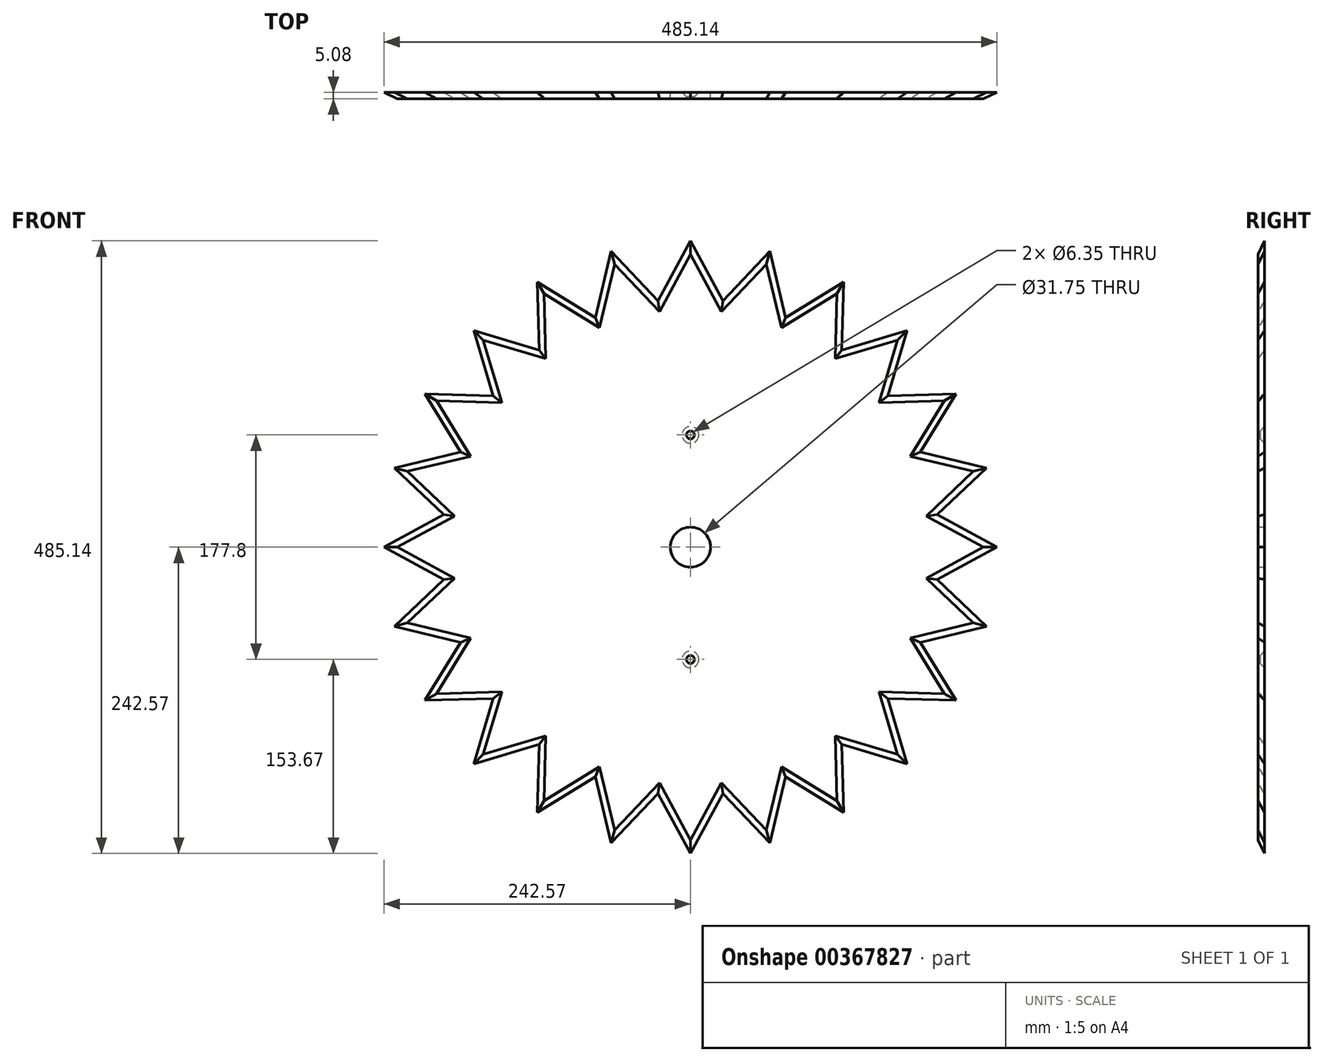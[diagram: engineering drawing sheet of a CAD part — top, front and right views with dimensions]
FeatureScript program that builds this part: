
annotation { "Feature Type Name" : "Feature", "Feature Type Description" : "" }
export const myFeature = defineFeature(function(context is Context, id is Id, definition is map)
    precondition{}
    {
        {
            var Q0;
            Q0=qCreatedBy(makeId("Front.planeOp"),FACE);
            var sketch = newSketch(context, id + "F0", { "sketchPlane" : qUnion([Q0])});
            skCircle(sketch, "E0", {"center": v(0, 0) * mm, "radius": 196.85 * mm});
            skLineSegment(sketch, "E1", {"start": v(0, 0) * mm, "end": v(0, 196.85) * mm, "construction": true});
            skLineSegment(sketch, "E2", {"start": v(0, 0) * mm, "end": v(50.95, 190.14) * mm, "construction": true});
            skLineSegment(sketch, "E3", {"start": v(0, 196.85) * mm, "end": v(0, 242.57) * mm, "construction": true});
            skLineSegment(sketch, "E4", {"start": v(0, 0) * mm, "end": v(25.7, 195.17) * mm, "construction": true});
            skLineSegment(sketch, "E5", {"start": v(0, 242.57) * mm, "end": v(25.7, 195.17) * mm});
            skLineSegment(sketch, "E6", {"start": v(50.95, 190.14) * mm, "end": v(62.78, 234.3) * mm, "construction": true});
            skLineSegment(sketch, "E7", {"start": v(25.7, 195.17) * mm, "end": v(62.78, 234.3) * mm});
            skLineSegment(sketch, "E8.1.0", {"start": v(62.78, 234.3) * mm, "end": v(75.33, 181.87) * mm});
            skLineSegment(sketch, "E8.1.1", {"start": v(75.33, 181.87) * mm, "end": v(121.28, 210.07) * mm});
            skLineSegment(sketch, "E8.2.0", {"start": v(121.29, 210.07) * mm, "end": v(119.83, 156.17) * mm});
            skLineSegment(sketch, "E8.2.1", {"start": v(119.83, 156.17) * mm, "end": v(171.52, 171.52) * mm});
            skLineSegment(sketch, "E8.3.0", {"start": v(171.52, 171.52) * mm, "end": v(156.17, 119.83) * mm});
            skLineSegment(sketch, "E8.3.1", {"start": v(156.17, 119.83) * mm, "end": v(210.07, 121.29) * mm});
            skLineSegment(sketch, "E8.4.0", {"start": v(210.07, 121.29) * mm, "end": v(181.87, 75.33) * mm});
            skLineSegment(sketch, "E8.4.1", {"start": v(181.87, 75.33) * mm, "end": v(234.3, 62.78) * mm});
            skLineSegment(sketch, "E8.5.0", {"start": v(234.3, 62.78) * mm, "end": v(195.17, 25.7) * mm});
            skLineSegment(sketch, "E8.5.1", {"start": v(195.17, 25.7) * mm, "end": v(242.57, 0) * mm});
            skLineSegment(sketch, "E8.6.0", {"start": v(242.57, 0) * mm, "end": v(195.17, -25.7) * mm});
            skLineSegment(sketch, "E8.6.1", {"start": v(195.17, -25.7) * mm, "end": v(234.3, -62.78) * mm});
            skLineSegment(sketch, "E8.7.0", {"start": v(234.3, -62.78) * mm, "end": v(181.87, -75.33) * mm});
            skLineSegment(sketch, "E8.7.1", {"start": v(181.87, -75.33) * mm, "end": v(210.07, -121.28) * mm});
            skLineSegment(sketch, "E8.8.0", {"start": v(210.07, -121.28) * mm, "end": v(156.17, -119.83) * mm});
            skLineSegment(sketch, "E8.8.1", {"start": v(156.17, -119.83) * mm, "end": v(171.52, -171.52) * mm});
            skLineSegment(sketch, "E8.9.0", {"start": v(171.52, -171.52) * mm, "end": v(119.83, -156.17) * mm});
            skLineSegment(sketch, "E8.9.1", {"start": v(119.83, -156.17) * mm, "end": v(121.29, -210.07) * mm});
            skLineSegment(sketch, "E8.10.0", {"start": v(121.29, -210.07) * mm, "end": v(75.33, -181.87) * mm});
            skLineSegment(sketch, "E8.10.1", {"start": v(75.33, -181.87) * mm, "end": v(62.78, -234.3) * mm});
            skLineSegment(sketch, "E8.11.0", {"start": v(62.78, -234.3) * mm, "end": v(25.7, -195.17) * mm});
            skLineSegment(sketch, "E8.11.1", {"start": v(25.7, -195.17) * mm, "end": v(0, -242.57) * mm});
            skLineSegment(sketch, "E8.12.0", {"start": v(0, -242.57) * mm, "end": v(-25.7, -195.17) * mm});
            skLineSegment(sketch, "E8.12.1", {"start": v(-25.7, -195.17) * mm, "end": v(-62.78, -234.3) * mm});
            skLineSegment(sketch, "E8.13.0", {"start": v(-62.78, -234.3) * mm, "end": v(-75.33, -181.87) * mm});
            skLineSegment(sketch, "E8.13.1", {"start": v(-75.33, -181.87) * mm, "end": v(-121.28, -210.07) * mm});
            skLineSegment(sketch, "E8.14.0", {"start": v(-121.28, -210.07) * mm, "end": v(-119.83, -156.17) * mm});
            skLineSegment(sketch, "E8.14.1", {"start": v(-119.83, -156.17) * mm, "end": v(-171.52, -171.52) * mm});
            skLineSegment(sketch, "E8.15.0", {"start": v(-171.52, -171.52) * mm, "end": v(-156.17, -119.83) * mm});
            skLineSegment(sketch, "E8.15.1", {"start": v(-156.17, -119.83) * mm, "end": v(-210.07, -121.29) * mm});
            skLineSegment(sketch, "E8.16.0", {"start": v(-210.07, -121.29) * mm, "end": v(-181.87, -75.33) * mm});
            skLineSegment(sketch, "E8.16.1", {"start": v(-181.87, -75.33) * mm, "end": v(-234.3, -62.78) * mm});
            skLineSegment(sketch, "E8.17.0", {"start": v(-234.3, -62.78) * mm, "end": v(-195.17, -25.7) * mm});
            skLineSegment(sketch, "E8.17.1", {"start": v(-195.17, -25.7) * mm, "end": v(-242.57, 0) * mm});
            skLineSegment(sketch, "E8.18.0", {"start": v(-242.57, 0) * mm, "end": v(-195.17, 25.7) * mm});
            skLineSegment(sketch, "E8.18.1", {"start": v(-195.17, 25.7) * mm, "end": v(-234.3, 62.78) * mm});
            skLineSegment(sketch, "E8.19.0", {"start": v(-234.3, 62.78) * mm, "end": v(-181.87, 75.33) * mm});
            skLineSegment(sketch, "E8.19.1", {"start": v(-181.87, 75.33) * mm, "end": v(-210.07, 121.29) * mm});
            skLineSegment(sketch, "E8.20.0", {"start": v(-210.07, 121.28) * mm, "end": v(-156.17, 119.83) * mm});
            skLineSegment(sketch, "E8.20.1", {"start": v(-156.17, 119.83) * mm, "end": v(-171.52, 171.52) * mm});
            skLineSegment(sketch, "E8.21.0", {"start": v(-171.52, 171.52) * mm, "end": v(-119.83, 156.17) * mm});
            skLineSegment(sketch, "E8.21.1", {"start": v(-119.83, 156.17) * mm, "end": v(-121.28, 210.07) * mm});
            skLineSegment(sketch, "E8.22.0", {"start": v(-121.29, 210.07) * mm, "end": v(-75.33, 181.87) * mm});
            skLineSegment(sketch, "E8.22.1", {"start": v(-75.33, 181.87) * mm, "end": v(-62.78, 234.3) * mm});
            skLineSegment(sketch, "E8.23.0", {"start": v(-62.78, 234.3) * mm, "end": v(-25.7, 195.17) * mm});
            skLineSegment(sketch, "E8.23.1", {"start": v(-25.7, 195.17) * mm, "end": v(0, 242.57) * mm});
            skLineSegment(sketch, "E8.anchor2", {"start": v(0, 0) * mm, "end": v(-25.7, 195.17) * mm, "construction": true});
            skSolve(sketch);
        }
        {
            var Q0;
            {var subQ0=sQuery(id+"F0.wireOp",EDGE,"E8.4.1");Q0=makeQuery(id+"F0.imprint","IMPRINT",FACE,{"disambiguationData":[TD([[makeQuery(id+"F0.imprint","IMPRINT",EDGE,{"derivedFrom":subQ0}),-1.0]])]});}
            var Q1;
            {var subQ0=sQuery(id+"F0.wireOp",EDGE,"E8.3.1");Q1=makeQuery(id+"F0.imprint","IMPRINT",FACE,{"disambiguationData":[TD([[makeQuery(id+"F0.imprint","IMPRINT",EDGE,{"derivedFrom":subQ0}),-1.0]])]});}
            var Q2;
            {var subQ0=sQuery(id+"F0.wireOp",EDGE,"E8.2.1");Q2=makeQuery(id+"F0.imprint","IMPRINT",FACE,{"disambiguationData":[TD([[makeQuery(id+"F0.imprint","IMPRINT",EDGE,{"derivedFrom":subQ0}),-1.0]])]});}
            var Q3;
            {var subQ0=sQuery(id+"F0.wireOp",EDGE,"E8.1.1");Q3=makeQuery(id+"F0.imprint","IMPRINT",FACE,{"disambiguationData":[TD([[makeQuery(id+"F0.imprint","IMPRINT",EDGE,{"derivedFrom":subQ0}),-1.0]])]});}
            var Q4;
            {var subQ0=sQuery(id+"F0.wireOp",EDGE,"E7");Q4=makeQuery(id+"F0.imprint","IMPRINT",FACE,{"disambiguationData":[TD([[makeQuery(id+"F0.imprint","IMPRINT",EDGE,{"derivedFrom":subQ0}),-1.0]])]});}
            var Q5;
            {var subQ0=sQuery(id+"F0.wireOp",EDGE,"E5");Q5=makeQuery(id+"F0.imprint","IMPRINT",FACE,{"disambiguationData":[TD([[makeQuery(id+"F0.imprint","IMPRINT",EDGE,{"derivedFrom":subQ0}),-1.0]])]});}
            var Q6;
            {var subQ0=sQuery(id+"F0.wireOp",EDGE,"E8.22.1");Q6=makeQuery(id+"F0.imprint","IMPRINT",FACE,{"disambiguationData":[TD([[makeQuery(id+"F0.imprint","IMPRINT",EDGE,{"derivedFrom":subQ0}),-1.0]])]});}
            var Q7;
            {var subQ0=sQuery(id+"F0.wireOp",EDGE,"E8.21.1");Q7=makeQuery(id+"F0.imprint","IMPRINT",FACE,{"disambiguationData":[TD([[makeQuery(id+"F0.imprint","IMPRINT",EDGE,{"derivedFrom":subQ0}),-1.0]])]});}
            var Q8;
            {var subQ0=sQuery(id+"F0.wireOp",EDGE,"E8.20.1");Q8=makeQuery(id+"F0.imprint","IMPRINT",FACE,{"disambiguationData":[TD([[makeQuery(id+"F0.imprint","IMPRINT",EDGE,{"derivedFrom":subQ0}),-1.0]])]});}
            var Q9;
            {var subQ0=sQuery(id+"F0.wireOp",EDGE,"E8.19.1");Q9=makeQuery(id+"F0.imprint","IMPRINT",FACE,{"disambiguationData":[TD([[makeQuery(id+"F0.imprint","IMPRINT",EDGE,{"derivedFrom":subQ0}),-1.0]])]});}
            var Q10;
            {var subQ0=sQuery(id+"F0.wireOp",EDGE,"E8.18.1");Q10=makeQuery(id+"F0.imprint","IMPRINT",FACE,{"disambiguationData":[TD([[makeQuery(id+"F0.imprint","IMPRINT",EDGE,{"derivedFrom":subQ0}),-1.0]])]});}
            var Q11;
            {var subQ0=sQuery(id+"F0.wireOp",EDGE,"E8.17.1");Q11=makeQuery(id+"F0.imprint","IMPRINT",FACE,{"disambiguationData":[TD([[makeQuery(id+"F0.imprint","IMPRINT",EDGE,{"derivedFrom":subQ0}),-1.0]])]});}
            var Q12;
            {var subQ0=sQuery(id+"F0.wireOp",EDGE,"E8.16.1");Q12=makeQuery(id+"F0.imprint","IMPRINT",FACE,{"disambiguationData":[TD([[makeQuery(id+"F0.imprint","IMPRINT",EDGE,{"derivedFrom":subQ0}),-1.0]])]});}
            var Q13;
            {var subQ0=sQuery(id+"F0.wireOp",EDGE,"E8.15.1");Q13=makeQuery(id+"F0.imprint","IMPRINT",FACE,{"disambiguationData":[TD([[makeQuery(id+"F0.imprint","IMPRINT",EDGE,{"derivedFrom":subQ0}),-1.0]])]});}
            var Q14;
            {var subQ0=sQuery(id+"F0.wireOp",EDGE,"E8.14.1");Q14=makeQuery(id+"F0.imprint","IMPRINT",FACE,{"disambiguationData":[TD([[makeQuery(id+"F0.imprint","IMPRINT",EDGE,{"derivedFrom":subQ0}),-1.0]])]});}
            var Q15;
            {var subQ0=sQuery(id+"F0.wireOp",EDGE,"E8.13.1");Q15=makeQuery(id+"F0.imprint","IMPRINT",FACE,{"disambiguationData":[TD([[makeQuery(id+"F0.imprint","IMPRINT",EDGE,{"derivedFrom":subQ0}),-1.0]])]});}
            var Q16;
            {var subQ0=sQuery(id+"F0.wireOp",EDGE,"E8.12.1");Q16=makeQuery(id+"F0.imprint","IMPRINT",FACE,{"disambiguationData":[TD([[makeQuery(id+"F0.imprint","IMPRINT",EDGE,{"derivedFrom":subQ0}),-1.0]])]});}
            var Q17;
            {var subQ0=sQuery(id+"F0.wireOp",EDGE,"E8.11.1");Q17=makeQuery(id+"F0.imprint","IMPRINT",FACE,{"disambiguationData":[TD([[makeQuery(id+"F0.imprint","IMPRINT",EDGE,{"derivedFrom":subQ0}),-1.0]])]});}
            var Q18;
            {var subQ0=sQuery(id+"F0.wireOp",EDGE,"E8.10.1");Q18=makeQuery(id+"F0.imprint","IMPRINT",FACE,{"disambiguationData":[TD([[makeQuery(id+"F0.imprint","IMPRINT",EDGE,{"derivedFrom":subQ0}),-1.0]])]});}
            var Q19;
            {var subQ0=sQuery(id+"F0.wireOp",EDGE,"E8.9.1");Q19=makeQuery(id+"F0.imprint","IMPRINT",FACE,{"disambiguationData":[TD([[makeQuery(id+"F0.imprint","IMPRINT",EDGE,{"derivedFrom":subQ0}),-1.0]])]});}
            var Q20;
            {var subQ0=sQuery(id+"F0.wireOp",EDGE,"E8.8.1");Q20=makeQuery(id+"F0.imprint","IMPRINT",FACE,{"disambiguationData":[TD([[makeQuery(id+"F0.imprint","IMPRINT",EDGE,{"derivedFrom":subQ0}),-1.0]])]});}
            var Q21;
            {var subQ0=sQuery(id+"F0.wireOp",EDGE,"E8.7.1");Q21=makeQuery(id+"F0.imprint","IMPRINT",FACE,{"disambiguationData":[TD([[makeQuery(id+"F0.imprint","IMPRINT",EDGE,{"derivedFrom":subQ0}),-1.0]])]});}
            var Q22;
            {var subQ0=sQuery(id+"F0.wireOp",EDGE,"E8.6.1");Q22=makeQuery(id+"F0.imprint","IMPRINT",FACE,{"disambiguationData":[TD([[makeQuery(id+"F0.imprint","IMPRINT",EDGE,{"derivedFrom":subQ0}),-1.0]])]});}
            var Q23;
            {var subQ0=sQuery(id+"F0.wireOp",EDGE,"E8.5.1");Q23=makeQuery(id+"F0.imprint","IMPRINT",FACE,{"disambiguationData":[TD([[makeQuery(id+"F0.imprint","IMPRINT",EDGE,{"derivedFrom":subQ0}),-1.0]])]});}
            var Q24;
            {var subQ0=sQuery(id+"F0.wireOp",EDGE,"E0");var subQ17=makeQuery(id+"F0.imprint","INTERSECT",VERTEX,{"derivedFrom":[subQ0,sQuery(id+"F0.wireOp",EDGE,"E8.4.0"),sQuery(id+"F0.wireOp",EDGE,"E8.4.1")]});Q24=makeQuery(id+"F0.imprint","IMPRINT",FACE,{"disambiguationData":[TD([[makeQuery(id+"F0.imprint","IMPRINT",EDGE,{"disambiguationData":[TD([[subQ17,1.0]])],"derivedFrom":subQ0}),1.0]])]});}
            extrude(context, id + "F1", {"entities" : qUnion([Q0, Q1, Q2, Q3, Q4, Q5, Q6, Q7, Q8, Q9, Q10, Q11, Q12, Q13, Q14, Q15, Q16, Q17, Q18, Q19, Q20, Q21, Q22, Q23, Q24]), "depth" : 5.08 * mm});
        }
        {
            var Q0;
            Q0=makeQuery(id+"F1.opExtrude","CAP_FACE",FACE,{"disambiguationData":[OSD([sQuery(id+"F0.wireOp",EDGE,"E5"),sQuery(id+"F0.wireOp",EDGE,"E7"),sQuery(id+"F0.wireOp",EDGE,"E8.1.0"),sQuery(id+"F0.wireOp",EDGE,"E8.1.1"),sQuery(id+"F0.wireOp",EDGE,"E8.2.0"),sQuery(id+"F0.wireOp",EDGE,"E8.2.1"),sQuery(id+"F0.wireOp",EDGE,"E8.3.0"),sQuery(id+"F0.wireOp",EDGE,"E8.3.1"),sQuery(id+"F0.wireOp",EDGE,"E8.4.0"),sQuery(id+"F0.wireOp",EDGE,"E8.4.1"),sQuery(id+"F0.wireOp",EDGE,"E8.5.0"),sQuery(id+"F0.wireOp",EDGE,"E8.5.1"),sQuery(id+"F0.wireOp",EDGE,"E8.6.0"),sQuery(id+"F0.wireOp",EDGE,"E8.6.1"),sQuery(id+"F0.wireOp",EDGE,"E8.7.0"),sQuery(id+"F0.wireOp",EDGE,"E8.7.1"),sQuery(id+"F0.wireOp",EDGE,"E8.8.0"),sQuery(id+"F0.wireOp",EDGE,"E8.8.1"),sQuery(id+"F0.wireOp",EDGE,"E8.9.0"),sQuery(id+"F0.wireOp",EDGE,"E8.9.1"),sQuery(id+"F0.wireOp",EDGE,"E8.10.0"),sQuery(id+"F0.wireOp",EDGE,"E8.10.1"),sQuery(id+"F0.wireOp",EDGE,"E8.11.0"),sQuery(id+"F0.wireOp",EDGE,"E8.11.1"),sQuery(id+"F0.wireOp",EDGE,"E8.12.0"),sQuery(id+"F0.wireOp",EDGE,"E8.12.1"),sQuery(id+"F0.wireOp",EDGE,"E8.13.0"),sQuery(id+"F0.wireOp",EDGE,"E8.13.1"),sQuery(id+"F0.wireOp",EDGE,"E8.14.0"),sQuery(id+"F0.wireOp",EDGE,"E8.14.1"),sQuery(id+"F0.wireOp",EDGE,"E8.15.0"),sQuery(id+"F0.wireOp",EDGE,"E8.15.1"),sQuery(id+"F0.wireOp",EDGE,"E8.16.0"),sQuery(id+"F0.wireOp",EDGE,"E8.16.1"),sQuery(id+"F0.wireOp",EDGE,"E8.17.0"),sQuery(id+"F0.wireOp",EDGE,"E8.17.1"),sQuery(id+"F0.wireOp",EDGE,"E8.18.0"),sQuery(id+"F0.wireOp",EDGE,"E8.18.1"),sQuery(id+"F0.wireOp",EDGE,"E8.19.0"),sQuery(id+"F0.wireOp",EDGE,"E8.19.1"),sQuery(id+"F0.wireOp",EDGE,"E8.20.0"),sQuery(id+"F0.wireOp",EDGE,"E8.20.1"),sQuery(id+"F0.wireOp",EDGE,"E8.21.0"),sQuery(id+"F0.wireOp",EDGE,"E8.21.1"),sQuery(id+"F0.wireOp",EDGE,"E8.22.0"),sQuery(id+"F0.wireOp",EDGE,"E8.22.1"),sQuery(id+"F0.wireOp",EDGE,"E8.23.0"),sQuery(id+"F0.wireOp",EDGE,"E8.23.1"),sQuery(id+"F0.wireOp",EDGE,"usub8CC4-KVD4-KCSl-eUXN-U1PbMKN3omxB"),sQuery(id+"F0.wireOp",EDGE,"0e038de5-12ab-48f5-9b6f-ffaeae1e67590.MirrorC")])],"isStart":false});
            chamfer(context, id + "F2", {"entities" : qUnion([Q0]), "width" : 5.08 * mm, "tangentPropagation" : true});
        }
        {
            var Q0;
            Q0=makeQuery(id+"F1.opExtrude","CAP_FACE",FACE,{"disambiguationData":[OSD([sQuery(id+"F0.wireOp",EDGE,"E5"),sQuery(id+"F0.wireOp",EDGE,"E7"),sQuery(id+"F0.wireOp",EDGE,"E8.1.0"),sQuery(id+"F0.wireOp",EDGE,"E8.1.1"),sQuery(id+"F0.wireOp",EDGE,"E8.2.0"),sQuery(id+"F0.wireOp",EDGE,"E8.2.1"),sQuery(id+"F0.wireOp",EDGE,"E8.3.0"),sQuery(id+"F0.wireOp",EDGE,"E8.3.1"),sQuery(id+"F0.wireOp",EDGE,"E8.4.0"),sQuery(id+"F0.wireOp",EDGE,"E8.4.1"),sQuery(id+"F0.wireOp",EDGE,"E8.5.0"),sQuery(id+"F0.wireOp",EDGE,"E8.5.1"),sQuery(id+"F0.wireOp",EDGE,"E8.6.0"),sQuery(id+"F0.wireOp",EDGE,"E8.6.1"),sQuery(id+"F0.wireOp",EDGE,"E8.7.0"),sQuery(id+"F0.wireOp",EDGE,"E8.7.1"),sQuery(id+"F0.wireOp",EDGE,"E8.8.0"),sQuery(id+"F0.wireOp",EDGE,"E8.8.1"),sQuery(id+"F0.wireOp",EDGE,"E8.9.0"),sQuery(id+"F0.wireOp",EDGE,"E8.9.1"),sQuery(id+"F0.wireOp",EDGE,"E8.10.0"),sQuery(id+"F0.wireOp",EDGE,"E8.10.1"),sQuery(id+"F0.wireOp",EDGE,"E8.11.0"),sQuery(id+"F0.wireOp",EDGE,"E8.11.1"),sQuery(id+"F0.wireOp",EDGE,"E8.12.0"),sQuery(id+"F0.wireOp",EDGE,"E8.12.1"),sQuery(id+"F0.wireOp",EDGE,"E8.13.0"),sQuery(id+"F0.wireOp",EDGE,"E8.13.1"),sQuery(id+"F0.wireOp",EDGE,"E8.14.0"),sQuery(id+"F0.wireOp",EDGE,"E8.14.1"),sQuery(id+"F0.wireOp",EDGE,"E8.15.0"),sQuery(id+"F0.wireOp",EDGE,"E8.15.1"),sQuery(id+"F0.wireOp",EDGE,"E8.16.0"),sQuery(id+"F0.wireOp",EDGE,"E8.16.1"),sQuery(id+"F0.wireOp",EDGE,"E8.17.0"),sQuery(id+"F0.wireOp",EDGE,"E8.17.1"),sQuery(id+"F0.wireOp",EDGE,"E8.18.0"),sQuery(id+"F0.wireOp",EDGE,"E8.18.1"),sQuery(id+"F0.wireOp",EDGE,"E8.19.0"),sQuery(id+"F0.wireOp",EDGE,"E8.19.1"),sQuery(id+"F0.wireOp",EDGE,"E8.20.0"),sQuery(id+"F0.wireOp",EDGE,"E8.20.1"),sQuery(id+"F0.wireOp",EDGE,"E8.21.0"),sQuery(id+"F0.wireOp",EDGE,"E8.21.1"),sQuery(id+"F0.wireOp",EDGE,"E8.22.0"),sQuery(id+"F0.wireOp",EDGE,"E8.22.1"),sQuery(id+"F0.wireOp",EDGE,"E8.23.0"),sQuery(id+"F0.wireOp",EDGE,"E8.23.1")])],"isStart":true});
            var sketch = newSketch(context, id + "F3", { "sketchPlane" : qUnion([Q0])});
            skCircle(sketch, "E9", {"center": v(0, 88.9) * mm, "radius": 6.35 * mm});
            skCircle(sketch, "E10.MirrorC", {"center": v(0, -88.9) * mm, "radius": 6.35 * mm});
            skSolve(sketch);
        }
        {
            var Q0;
            Q0=sQuery(id+"F3.wireOp",VERTEX,"E9.center");
            var Q1;
            Q1=sQuery(id+"F3.wireOp",VERTEX,"E10.MirrorC.center");
            var Q2;
            Q2=makeQuery(id+"F1.opExtrude","SWEPT_BODY",BODY,{"disambiguationData":[OSD([sQuery(id+"F0.wireOp",EDGE,"E5"),sQuery(id+"F0.wireOp",EDGE,"E7"),sQuery(id+"F0.wireOp",EDGE,"E8.1.0"),sQuery(id+"F0.wireOp",EDGE,"E8.1.1"),sQuery(id+"F0.wireOp",EDGE,"E8.2.0"),sQuery(id+"F0.wireOp",EDGE,"E8.2.1"),sQuery(id+"F0.wireOp",EDGE,"E8.3.0"),sQuery(id+"F0.wireOp",EDGE,"E8.3.1"),sQuery(id+"F0.wireOp",EDGE,"E8.4.0"),sQuery(id+"F0.wireOp",EDGE,"E8.4.1"),sQuery(id+"F0.wireOp",EDGE,"E8.5.0"),sQuery(id+"F0.wireOp",EDGE,"E8.5.1"),sQuery(id+"F0.wireOp",EDGE,"E8.6.0"),sQuery(id+"F0.wireOp",EDGE,"E8.6.1"),sQuery(id+"F0.wireOp",EDGE,"E8.7.0"),sQuery(id+"F0.wireOp",EDGE,"E8.7.1"),sQuery(id+"F0.wireOp",EDGE,"E8.8.0"),sQuery(id+"F0.wireOp",EDGE,"E8.8.1"),sQuery(id+"F0.wireOp",EDGE,"E8.9.0"),sQuery(id+"F0.wireOp",EDGE,"E8.9.1"),sQuery(id+"F0.wireOp",EDGE,"E8.10.0"),sQuery(id+"F0.wireOp",EDGE,"E8.10.1"),sQuery(id+"F0.wireOp",EDGE,"E8.11.0"),sQuery(id+"F0.wireOp",EDGE,"E8.11.1"),sQuery(id+"F0.wireOp",EDGE,"E8.12.0"),sQuery(id+"F0.wireOp",EDGE,"E8.12.1"),sQuery(id+"F0.wireOp",EDGE,"E8.13.0"),sQuery(id+"F0.wireOp",EDGE,"E8.13.1"),sQuery(id+"F0.wireOp",EDGE,"E8.14.0"),sQuery(id+"F0.wireOp",EDGE,"E8.14.1"),sQuery(id+"F0.wireOp",EDGE,"E8.15.0"),sQuery(id+"F0.wireOp",EDGE,"E8.15.1"),sQuery(id+"F0.wireOp",EDGE,"E8.16.0"),sQuery(id+"F0.wireOp",EDGE,"E8.16.1"),sQuery(id+"F0.wireOp",EDGE,"E8.17.0"),sQuery(id+"F0.wireOp",EDGE,"E8.17.1"),sQuery(id+"F0.wireOp",EDGE,"E8.18.0"),sQuery(id+"F0.wireOp",EDGE,"E8.18.1"),sQuery(id+"F0.wireOp",EDGE,"E8.19.0"),sQuery(id+"F0.wireOp",EDGE,"E8.19.1"),sQuery(id+"F0.wireOp",EDGE,"E8.20.0"),sQuery(id+"F0.wireOp",EDGE,"E8.20.1"),sQuery(id+"F0.wireOp",EDGE,"E8.21.0"),sQuery(id+"F0.wireOp",EDGE,"E8.21.1"),sQuery(id+"F0.wireOp",EDGE,"E8.22.0"),sQuery(id+"F0.wireOp",EDGE,"E8.22.1"),sQuery(id+"F0.wireOp",EDGE,"E8.23.0"),sQuery(id+"F0.wireOp",EDGE,"E8.23.1")])]});
            hole(context, id + "F4", {"style" : HoleStyle.C_SINK, "endStyle" : HoleEndStyle.THROUGH, "holeDiameter" : 6.35 * mm, "cSinkDiameter" : 13.2 * mm, "cSinkAngle" : 90 * degree, "isTappedThrough" : true, "tappedDepth" : 12.7 * mm, "tapClearance" : 3, "locations" : qUnion([Q0, Q1]), "scope" : qUnion([Q2])});
        }
        {
            var Q0;
            Q0=makeQuery(id+"F1.opExtrude","CAP_FACE",FACE,{"disambiguationData":[OSD([sQuery(id+"F0.wireOp",EDGE,"E5"),sQuery(id+"F0.wireOp",EDGE,"E7"),sQuery(id+"F0.wireOp",EDGE,"E8.1.0"),sQuery(id+"F0.wireOp",EDGE,"E8.1.1"),sQuery(id+"F0.wireOp",EDGE,"E8.2.0"),sQuery(id+"F0.wireOp",EDGE,"E8.2.1"),sQuery(id+"F0.wireOp",EDGE,"E8.3.0"),sQuery(id+"F0.wireOp",EDGE,"E8.3.1"),sQuery(id+"F0.wireOp",EDGE,"E8.4.0"),sQuery(id+"F0.wireOp",EDGE,"E8.4.1"),sQuery(id+"F0.wireOp",EDGE,"E8.5.0"),sQuery(id+"F0.wireOp",EDGE,"E8.5.1"),sQuery(id+"F0.wireOp",EDGE,"E8.6.0"),sQuery(id+"F0.wireOp",EDGE,"E8.6.1"),sQuery(id+"F0.wireOp",EDGE,"E8.7.0"),sQuery(id+"F0.wireOp",EDGE,"E8.7.1"),sQuery(id+"F0.wireOp",EDGE,"E8.8.0"),sQuery(id+"F0.wireOp",EDGE,"E8.8.1"),sQuery(id+"F0.wireOp",EDGE,"E8.9.0"),sQuery(id+"F0.wireOp",EDGE,"E8.9.1"),sQuery(id+"F0.wireOp",EDGE,"E8.10.0"),sQuery(id+"F0.wireOp",EDGE,"E8.10.1"),sQuery(id+"F0.wireOp",EDGE,"E8.11.0"),sQuery(id+"F0.wireOp",EDGE,"E8.11.1"),sQuery(id+"F0.wireOp",EDGE,"E8.12.0"),sQuery(id+"F0.wireOp",EDGE,"E8.12.1"),sQuery(id+"F0.wireOp",EDGE,"E8.13.0"),sQuery(id+"F0.wireOp",EDGE,"E8.13.1"),sQuery(id+"F0.wireOp",EDGE,"E8.14.0"),sQuery(id+"F0.wireOp",EDGE,"E8.14.1"),sQuery(id+"F0.wireOp",EDGE,"E8.15.0"),sQuery(id+"F0.wireOp",EDGE,"E8.15.1"),sQuery(id+"F0.wireOp",EDGE,"E8.16.0"),sQuery(id+"F0.wireOp",EDGE,"E8.16.1"),sQuery(id+"F0.wireOp",EDGE,"E8.17.0"),sQuery(id+"F0.wireOp",EDGE,"E8.17.1"),sQuery(id+"F0.wireOp",EDGE,"E8.18.0"),sQuery(id+"F0.wireOp",EDGE,"E8.18.1"),sQuery(id+"F0.wireOp",EDGE,"E8.19.0"),sQuery(id+"F0.wireOp",EDGE,"E8.19.1"),sQuery(id+"F0.wireOp",EDGE,"E8.20.0"),sQuery(id+"F0.wireOp",EDGE,"E8.20.1"),sQuery(id+"F0.wireOp",EDGE,"E8.21.0"),sQuery(id+"F0.wireOp",EDGE,"E8.21.1"),sQuery(id+"F0.wireOp",EDGE,"E8.22.0"),sQuery(id+"F0.wireOp",EDGE,"E8.22.1"),sQuery(id+"F0.wireOp",EDGE,"E8.23.0"),sQuery(id+"F0.wireOp",EDGE,"E8.23.1")])],"isStart":true});
            var sketch = newSketch(context, id + "F5", { "sketchPlane" : qUnion([Q0])});
            skCircle(sketch, "E11", {"center": v(0, 0) * mm, "radius": 15.88 * mm});
            skSolve(sketch);
        }
        {
            var Q0;
            Q0 = qSketchRegion(id + "F5", true);
            extrude(context, id + "F6", {"entities" : qUnion([Q0]), "operationType" : NewBodyOperationType.REMOVE, "oppositeDirection" : true, "depth" : 25.4 * mm});
        }
    });
